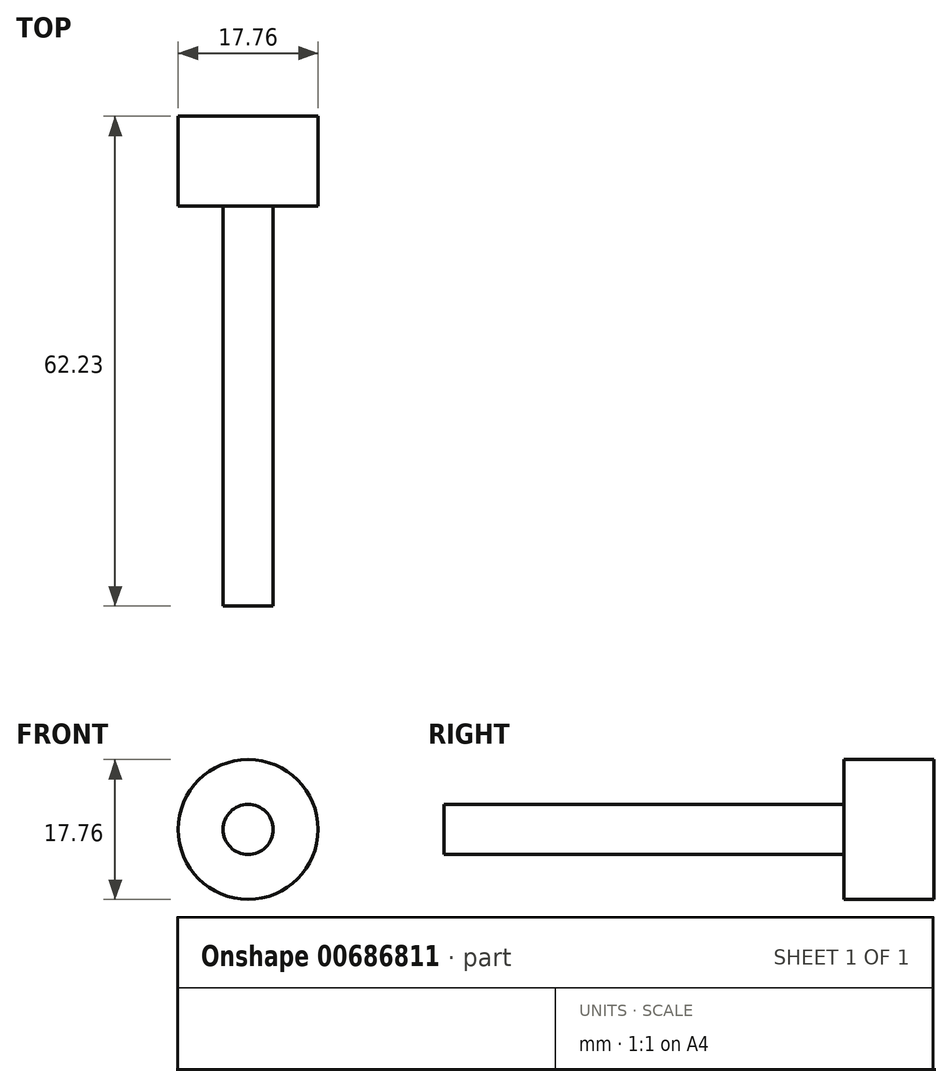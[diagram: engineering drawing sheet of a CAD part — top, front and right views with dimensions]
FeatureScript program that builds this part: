
annotation { "Feature Type Name" : "Feature", "Feature Type Description" : "" }
export const myFeature = defineFeature(function(context is Context, id is Id, definition is map)
    precondition{}
    {
        {
            var Q0;
            Q0=qCreatedBy(makeId("Front.planeOp"),FACE);
            var sketch = newSketch(context, id + "F0", { "sketchPlane" : qUnion([Q0])});
            skCircle(sketch, "E0", {"center": v(0, 0) * mm, "radius": 8.88 * mm});
            skSolve(sketch);
        }
        {
            var Q0;
            Q0=makeQuery(id+"F0.imprint","IMPRINT",FACE,{"disambiguationData":[TD([[makeQuery(id+"F0.imprint","IMPRINT",EDGE,{"derivedFrom":sQuery(id+"F0.wireOp",EDGE,"E0")}),1.0]])]});
            var Q1;
            Q1=sQuery(id+"F0.wireOp",EDGE,"E0");
            extrude(context, id + "F1", {"entities" : qUnion([Q0]), "surfaceEntities" : qUnion([Q1]), "depth" : 11.43 * mm, "offsetDistance" : 25.4 * mm});
        }
        {
            var Q0;
            Q0=makeQuery(id+"F1.opExtrude","CAP_FACE",FACE,{"disambiguationData":[OSD([sQuery(id+"F0.wireOp",EDGE,"E0")])],"isStart":false});
            var sketch = newSketch(context, id + "F2", { "sketchPlane" : qUnion([Q0])});
            skPoint(sketch, "E1", {"position": v(0, 0) * mm});
            skSolve(sketch);
        }
        {
            var Q0;
            Q0=makeQuery(id+"F2.imprint","IMPRINT",FACE,{"disambiguationData":[TD([[makeQuery(id+"F2.imprint","IMPRINT",EDGE,{"derivedFrom":makeQuery(id+"F1.opExtrude","CAP_EDGE",EDGE,{"disambiguationData":[OSD([sQuery(id+"F0.wireOp",EDGE,"E0")])],"isStart":false})}),1.0]])]});
            var sketch = newSketch(context, id + "F3", { "sketchPlane" : qUnion([Q0])});
            skCircle(sketch, "E2", {"center": v(0, 0) * mm, "radius": 3.18 * mm});
            skSolve(sketch);
        }
        {
            var Q0;
            Q0=makeQuery(id+"F3.imprint","IMPRINT",FACE,{"disambiguationData":[TD([[makeQuery(id+"F3.imprint","IMPRINT",EDGE,{"derivedFrom":sQuery(id+"F3.wireOp",EDGE,"E2")}),1.0]])]});
            var Q1;
            Q1=sQuery(id+"F3.wireOp",EDGE,"E2");
            extrude(context, id + "F4", {"entities" : qUnion([Q0]), "surfaceEntities" : qUnion([Q1]), "depth" : 50.8 * mm, "offsetDistance" : 25.4 * mm});
        }
    });
